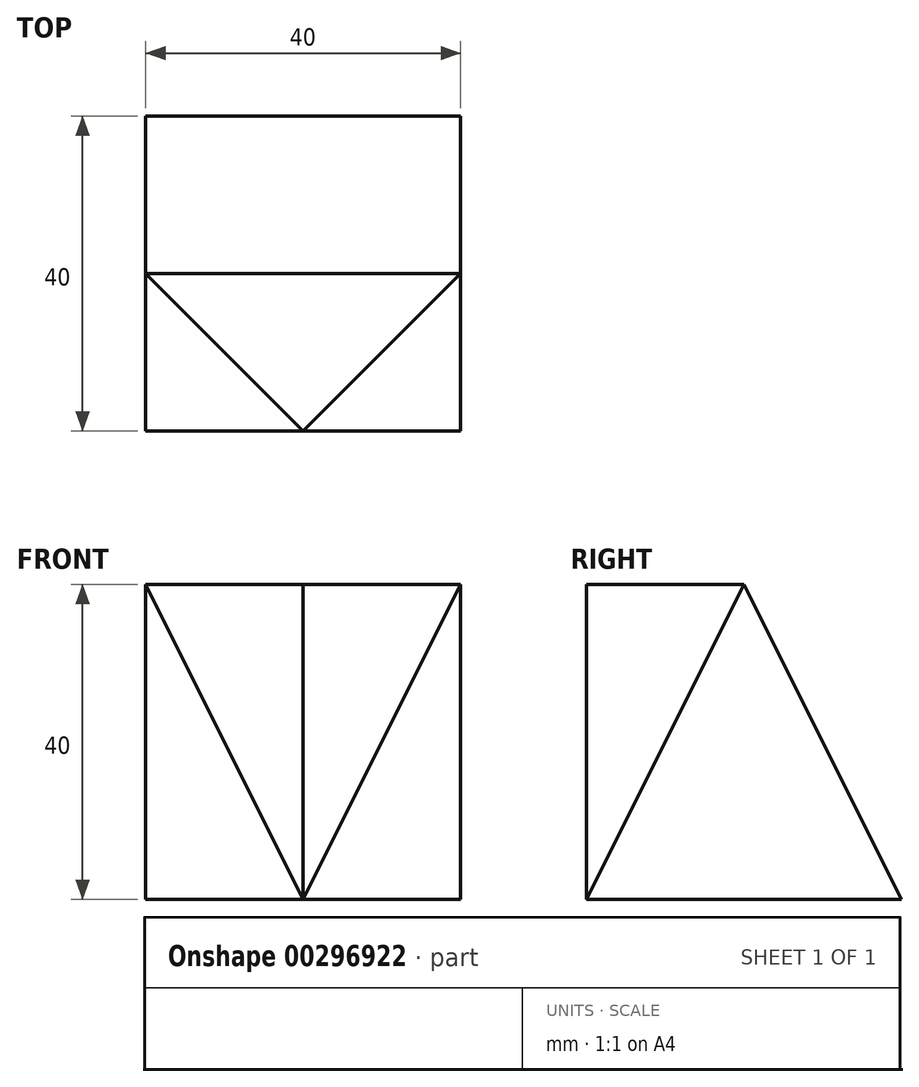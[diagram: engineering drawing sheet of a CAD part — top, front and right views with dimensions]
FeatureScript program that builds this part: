
annotation { "Feature Type Name" : "Feature", "Feature Type Description" : "" }
export const myFeature = defineFeature(function(context is Context, id is Id, definition is map)
    precondition{}
    {
        {
            var Q0;
            Q0=qCreatedBy(makeId("Right.planeOp"),FACE);
            var sketch = newSketch(context, id + "F0", { "sketchPlane" : qUnion([Q0])});
            skLineSegment(sketch, "E0.bottom", {"start": v(0, 0) * mm, "end": v(40, 0) * mm});
            skLineSegment(sketch, "E0.top", {"start": v(0, 40) * mm, "end": v(40, 40) * mm});
            skLineSegment(sketch, "E0.left", {"start": v(0, 0) * mm, "end": v(0, 40) * mm});
            skLineSegment(sketch, "E0.right", {"start": v(40, 0) * mm, "end": v(40, 40) * mm});
            skLineSegment(sketch, "E1", {"start": v(20, 40) * mm, "end": v(40, 0) * mm});
            skLineSegment(sketch, "E2", {"start": v(20, 40) * mm, "end": v(0, 0) * mm});
            skSolve(sketch);
        }
        {
            var Q0;
            Q0=makeQuery(id+"F0.imprint","IMPRINT",FACE,{"disambiguationData":[TD([[makeQuery(id+"F0.imprint","IMPRINT",EDGE,{"derivedFrom":sQuery(id+"F0.wireOp",EDGE,"E0.bottom")}),1.0]])]});
            extrude(context, id + "F1", {"entities" : qUnion([Q0]), "depth" : 40 * mm, "symmetric" : true});
        }
        {
            var Q0;
            Q0=makeQuery(id+"F1.opExtrude","SWEPT_FACE",FACE,{"disambiguationData":[OSD([sQuery(id+"F0.wireOp",EDGE,"E0.bottom")])]});
            var sketch = newSketch(context, id + "F2", { "sketchPlane" : qUnion([Q0])});
            skLineSegment(sketch, "E3", {"start": v(0, 0) * mm, "end": v(-20, -20) * mm});
            skLineSegment(sketch, "E4", {"start": v(-20, -20) * mm, "end": v(0, -40) * mm});
            skLineSegment(sketch, "E5", {"start": v(0, -40) * mm, "end": v(20, -20) * mm});
            skLineSegment(sketch, "E6", {"start": v(20, -20) * mm, "end": v(0, 0) * mm});
            skLineSegment(sketch, "E7", {"start": v(-20, -20) * mm, "end": v(20, -20) * mm});
            skSolve(sketch);
        }
        {
            var Q0;
            Q0=makeQuery(id+"F2.imprint","IMPRINT",FACE,{"disambiguationData":[TD([[makeQuery(id+"F2.imprint","IMPRINT",EDGE,{"derivedFrom":sQuery(id+"F2.wireOp",EDGE,"E3")}),1.0]])]});
            extrude(context, id + "F3", {"entities" : qUnion([Q0]), "operationType" : NewBodyOperationType.ADD, "oppositeDirection" : true, "depth" : 40 * mm});
        }
    });
